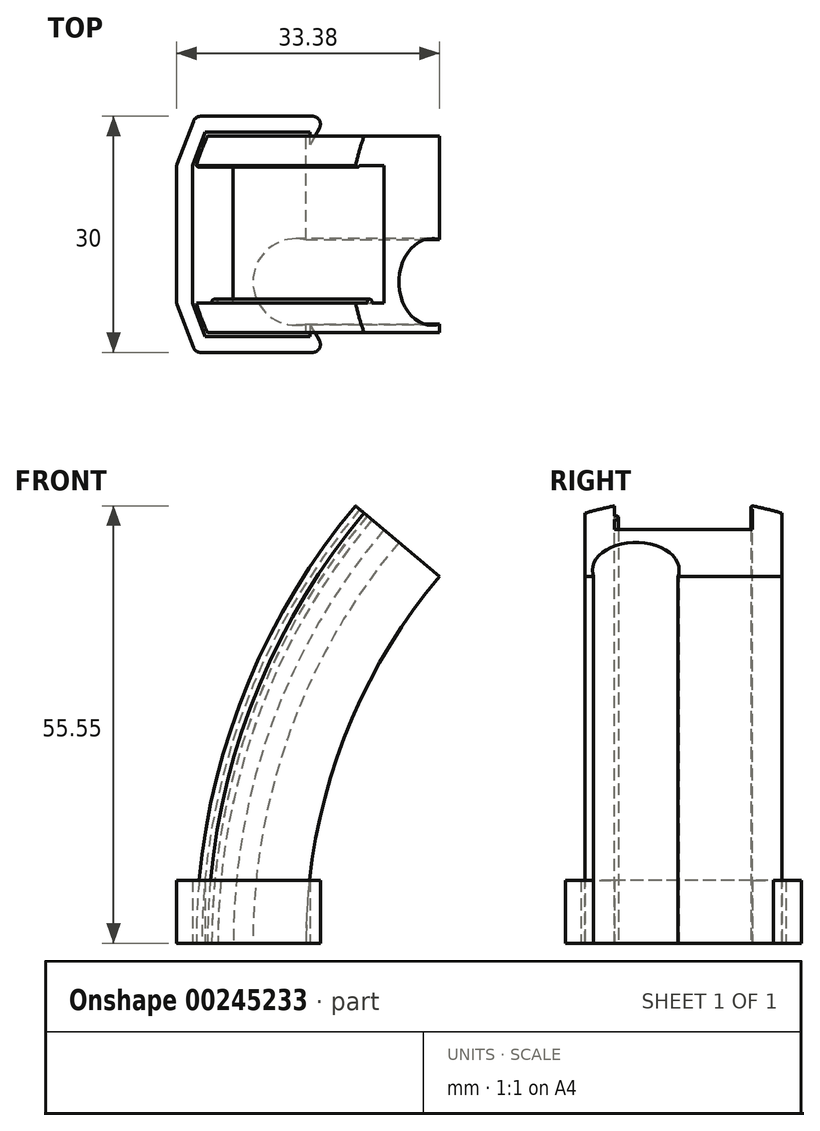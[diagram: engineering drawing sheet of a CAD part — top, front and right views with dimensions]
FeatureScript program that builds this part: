
annotation { "Feature Type Name" : "Feature", "Feature Type Description" : "" }
export const myFeature = defineFeature(function(context is Context, id is Id, definition is map)
    precondition{}
    {
        {
            var Q0;
            Q0=qCreatedBy(makeId("Front.planeOp"),FACE);
            var sketch = newSketch(context, id + "F0", { "sketchPlane" : qUnion([Q0])});
            skLineSegment(sketch, "E0", {"start": v(-8.16, 0) * mm, "end": v(70.34, 0) * mm, "construction": true});
            skArc(sketch, "E1", {"start": v(10.2, 50.46) * mm, "mid": v(-3.42, 26.85) * mm, "end": v(-8.16, 0) * mm});
            skArc(sketch, "E2", {"start": v(5.23, 54.64) * mm, "mid": v(-9.53, 29.07) * mm, "end": v(-14.66, 0) * mm});
            skLineSegment(sketch, "E3", {"start": v(10.2, 50.46) * mm, "end": v(70.34, 0) * mm, "construction": true});
            skLineSegment(sketch, "E4", {"start": v(-14.66, 0) * mm, "end": v(-8.16, 0) * mm});
            skLineSegment(sketch, "E5", {"start": v(10.2, 50.46) * mm, "end": v(5.23, 54.64) * mm});
            skSolve(sketch);
        }
        {
            var Q0;
            Q0 = qSketchRegion(id + "F0", true);
            extrude(context, id + "F1", {"entities" : qUnion([Q0]), "depth" : 25 * mm});
        }
        {
            var Q0;
            Q0=makeQuery(id+"F1.opExtrude","CAP_EDGE",EDGE,{"disambiguationData":[OSD([sQuery(id+"F0.wireOp",EDGE,"E1")])],"isStart":false});
            var Q1;
            Q1=makeQuery(id+"F1.opExtrude","CAP_VERTEX",VERTEX,{"disambiguationData":[OSD([sQuery(id+"F0.wireOp",EDGE,"E1"),sQuery(id+"F0.wireOp",EDGE,"E4")])],"isStart":false});
            cPlane(context, id + "F2", {"entities" : qUnion([Q0, Q1]), "cplaneType" : CPlaneType.CURVE_POINT, "offset" : 25 * mm, "width" : 150 * mm, "height" : 150 * mm});
        }
        {
            var Q0;
            Q0=qCreatedBy(id+"F2.planeOp",FACE);
            var sketch = newSketch(context, id + "F3", { "sketchPlane" : qUnion([Q0])});
            skPoint(sketch, "E6.0", {"position": v(-14.66, 25) * mm});
            skPoint(sketch, "E7.0", {"position": v(-8.16, 25) * mm});
            skPoint(sketch, "E8.0", {"position": v(-8.16, 12.5) * mm});
            skPoint(sketch, "E9.0", {"position": v(-14.66, 12.5) * mm});
            skLineSegment(sketch, "E10", {"start": v(-14.66, 12.5) * mm, "end": v(-8.16, 12.5) * mm, "construction": true});
            skArc(sketch, "E11", {"start": v(-14.66, 25) * mm, "mid": v(-17.39, 12.5) * mm, "end": v(-14.66, 0) * mm});
            skLineSegment(sketch, "E12", {"start": v(-14.66, 25) * mm, "end": v(-14.66, 0) * mm});
            skLineSegment(sketch, "E13", {"start": v(-8.16, 25) * mm, "end": v(-2.16, 25) * mm});
            skLineSegment(sketch, "E14.MirrorCS", {"start": v(-8.16, 0) * mm, "end": v(-2.16, 0) * mm});
            skLineSegment(sketch, "E15", {"start": v(-8.16, 25) * mm, "end": v(-8.16, 0) * mm});
            skLineSegment(sketch, "E16", {"start": v(-2.16, 25) * mm, "end": v(-2.16, 0) * mm});
            skSolve(sketch);
        }
        {
            var Q0;
            Q0=makeQuery(id+"F3.imprint","IMPRINT",FACE,{"disambiguationData":[TD([[makeQuery(id+"F3.imprint","IMPRINT",EDGE,{"derivedFrom":sQuery(id+"F3.wireOp",EDGE,"E11")}),1.0]])]});
            var Q1;
            Q1=makeQuery(id+"F3.imprint","IMPRINT",FACE,{"disambiguationData":[TD([[makeQuery(id+"F3.imprint","IMPRINT",EDGE,{"derivedFrom":sQuery(id+"F3.wireOp",EDGE,"E13")}),-1.0]])]});
            var Q2;
            Q2=makeQuery(id+"F1.opExtrude","CAP_EDGE",EDGE,{"disambiguationData":[OSD([sQuery(id+"F0.wireOp",EDGE,"E1")])],"isStart":false});
            sweep(context, id + "F4", {"operationType" : NewBodyOperationType.ADD, "profiles" : qUnion([Q0, Q1]), "path" : qUnion([Q2])});
        }
        {
            var Q0;
            {var subQ0=sQuery(id+"F0.wireOp",EDGE,"E4");var subQ1=sQuery(id+"F0.wireOp",EDGE,"E1");Q0=makeQuery(id+"F4.boolean.opBoolean","MERGE",FACE,{"derivedFrom":[makeQuery(id+"F1.opExtrude","SWEPT_FACE",FACE,{"disambiguationData":[OSD([subQ0])]}),makeQuery(id+"F4.opSweep","CAP_FACE",FACE,{"disambiguationData":[OSD([subQ1,subQ0,sQuery(id+"F3.wireOp",EDGE,"E11"),sQuery(id+"F3.wireOp",EDGE,"E12")])],"isStart":true}),makeQuery(id+"F4.opSweep","CAP_FACE",FACE,{"disambiguationData":[OSD([subQ1,subQ0,sQuery(id+"F3.wireOp",EDGE,"E13"),sQuery(id+"F3.wireOp",EDGE,"E14.MirrorCS"),sQuery(id+"F3.wireOp",EDGE,"E15"),sQuery(id+"F3.wireOp",EDGE,"OGJAd92x-gfcs-rjC3-avb7-BWxVoqmYbHhy")])],"isStart":true})]});}
            var sketch = newSketch(context, id + "F5", { "sketchPlane" : qUnion([Q0])});
            skCircle(sketch, "E17", {"center": v(-3.39, 18.55) * mm, "radius": 5.5 * mm});
            skLineSegment(sketch, "E18", {"start": v(-17.39, 12.5) * mm, "end": v(-17.39, 12.5) * mm});
            skCircle(sketch, "E19.MirrorC", {"center": v(-3.39, 6.45) * mm, "radius": 5.5 * mm});
            skLineSegment(sketch, "E20.bottom", {"start": v(-17.39, 21.25) * mm, "end": v(-11.39, 21.25) * mm});
            skLineSegment(sketch, "E20.top", {"start": v(-17.39, 3.75) * mm, "end": v(-11.39, 3.75) * mm});
            skLineSegment(sketch, "E20.left", {"start": v(-17.39, 21.25) * mm, "end": v(-17.39, 3.75) * mm});
            skLineSegment(sketch, "E20.right", {"start": v(-11.39, 21.25) * mm, "end": v(-11.39, 3.75) * mm});
            skPoint(sketch, "E20.middle", {"position": v(-14.39, 12.5) * mm});
            skLineSegment(sketch, "E21", {"start": v(-11.39, 18.75) * mm, "end": v(-3.39, 18.55) * mm, "construction": true});
            skLineSegment(sketch, "E22", {"start": v(-11.39, 18.75) * mm, "end": v(-11.39, 21.25) * mm, "construction": true});
            skSolve(sketch);
        }
        {
            var Q0;
            {var subQ0=sQuery(id+"F5.wireOp",EDGE,"E17");var subQ1=makeQuery(id+"F4.opSweep","CAP_EDGE",EDGE,{"disambiguationData":[OSD([sQuery(id+"F0.wireOp",EDGE,"E1"),sQuery(id+"F0.wireOp",EDGE,"E4"),sQuery(id+"F3.wireOp",EDGE,"OGJAd92x-gfcs-rjC3-avb7-BWxVoqmYbHhy")])],"isStart":true});var subQ2=makeQuery(id+"F5.imprint","INTERSECT",VERTEX,{"disambiguationData":[OD(0.0)],"derivedFrom":[subQ1,subQ0]});Q0=makeQuery(id+"F5.imprint","IMPRINT",FACE,{"disambiguationData":[TD([[makeQuery(id+"F5.imprint","IMPRINT",EDGE,{"disambiguationData":[TD([[subQ2,-1.0]])],"derivedFrom":subQ0}),1.0]])]});}
            var Q1;
            {var subQ0=sQuery(id+"F5.wireOp",EDGE,"E19.MirrorC");var subQ1=makeQuery(id+"F4.opSweep","CAP_EDGE",EDGE,{"disambiguationData":[OSD([sQuery(id+"F0.wireOp",EDGE,"E1"),sQuery(id+"F0.wireOp",EDGE,"E4"),sQuery(id+"F3.wireOp",EDGE,"OGJAd92x-gfcs-rjC3-avb7-BWxVoqmYbHhy")])],"isStart":true});var subQ2=makeQuery(id+"F5.imprint","INTERSECT",VERTEX,{"disambiguationData":[OD(0.0)],"derivedFrom":[subQ1,subQ0]});Q1=makeQuery(id+"F5.imprint","IMPRINT",FACE,{"disambiguationData":[TD([[makeQuery(id+"F5.imprint","IMPRINT",EDGE,{"disambiguationData":[TD([[subQ2,-1.0]])],"derivedFrom":subQ0}),-1.0]])]});}
            var Q2;
            {var subQ4=sQuery(id+"F5.wireOp",EDGE,"E20.right");Q2=makeQuery(id+"F5.imprint","IMPRINT",FACE,{"disambiguationData":[TD([[makeQuery(id+"F5.imprint","IMPRINT",EDGE,{"derivedFrom":subQ4}),-1.0]])]});}
            var Q3;
            {var subQ0=sQuery(id+"F5.wireOp",EDGE,"E19.MirrorC");var subQ1=makeQuery(id+"F4.opSweep","CAP_EDGE",EDGE,{"disambiguationData":[OSD([sQuery(id+"F0.wireOp",EDGE,"E1"),sQuery(id+"F0.wireOp",EDGE,"E4"),sQuery(id+"F3.wireOp",EDGE,"E16")])],"isStart":true});var subQ2=makeQuery(id+"F5.imprint","INTERSECT",VERTEX,{"disambiguationData":[OD(0.0)],"derivedFrom":[subQ1,subQ0]});Q3=makeQuery(id+"F5.imprint","IMPRINT",FACE,{"disambiguationData":[TD([[makeQuery(id+"F5.imprint","IMPRINT",EDGE,{"disambiguationData":[TD([[subQ2,-1.0]])],"derivedFrom":subQ0}),-1.0]])]});}
            var Q4;
            {var subQ0=sQuery(id+"F5.wireOp",EDGE,"E17");var subQ1=makeQuery(id+"F4.opSweep","CAP_EDGE",EDGE,{"disambiguationData":[OSD([sQuery(id+"F0.wireOp",EDGE,"E1"),sQuery(id+"F0.wireOp",EDGE,"E4"),sQuery(id+"F3.wireOp",EDGE,"E16")])],"isStart":true});var subQ2=makeQuery(id+"F5.imprint","INTERSECT",VERTEX,{"disambiguationData":[OD(0.0)],"derivedFrom":[subQ1,subQ0]});Q4=makeQuery(id+"F5.imprint","IMPRINT",FACE,{"disambiguationData":[TD([[makeQuery(id+"F5.imprint","IMPRINT",EDGE,{"disambiguationData":[TD([[subQ2,-1.0]])],"derivedFrom":subQ0}),1.0]])]});}
            var Q5;
            Q5=makeQuery(id+"F4.opSweep","SWEPT_EDGE",EDGE,{"disambiguationData":[OSD([sQuery(id+"F0.wireOp",EDGE,"E1"),sQuery(id+"F3.wireOp",EDGE,"E13"),sQuery(id+"F3.wireOp",EDGE,"OGJAd92x-gfcs-rjC3-avb7-BWxVoqmYbHhy")])]});
            sweep(context, id + "F6", {"operationType" : NewBodyOperationType.REMOVE, "profiles" : qUnion([Q0, Q1, Q2, Q3, Q4]), "path" : qUnion([Q5])});
        }
        {
            var Q0;
            {var subQ0=sQuery(id+"F0.wireOp",EDGE,"E4");var subQ1=sQuery(id+"F0.wireOp",EDGE,"E1");Q0=makeQuery(id+"F4.boolean.opBoolean","MERGE",FACE,{"derivedFrom":[makeQuery(id+"F1.opExtrude","SWEPT_FACE",FACE,{"disambiguationData":[OSD([subQ0])]}),makeQuery(id+"F4.opSweep","CAP_FACE",FACE,{"disambiguationData":[OSD([subQ1,subQ0,sQuery(id+"F3.wireOp",EDGE,"E11"),sQuery(id+"F3.wireOp",EDGE,"E12")])],"isStart":true}),makeQuery(id+"F4.opSweep","CAP_FACE",FACE,{"disambiguationData":[OSD([subQ1,subQ0,sQuery(id+"F3.wireOp",EDGE,"E13"),sQuery(id+"F3.wireOp",EDGE,"E14.MirrorCS"),sQuery(id+"F3.wireOp",EDGE,"E15"),sQuery(id+"F3.wireOp",EDGE,"OGJAd92x-gfcs-rjC3-avb7-BWxVoqmYbHhy")])],"isStart":true})]});}
            var sketch = newSketch(context, id + "F7", { "sketchPlane" : qUnion([Q0])});
            skPoint(sketch, "E23.startSnap0", {"position": v(-15.43, 1.85) * mm});
            skArc(sketch, "E24", {"start": v(-15.38, 3.75) * mm, "mid": v(-15.73, 3.96) * mm, "end": v(-16.08, 3.75) * mm});
            skLineSegment(sketch, "E25", {"start": v(-15.73, 3.96) * mm, "end": v(-15.73, 3.56) * mm, "construction": true});
            skLineSegment(sketch, "E26", {"start": v(-13.73, 20.73) * mm, "end": v(-13.73, 21.13) * mm, "construction": true});
            skArc(sketch, "E27", {"start": v(-14.12, 21.25) * mm, "mid": v(-13.73, 20.73) * mm, "end": v(-13.35, 21.25) * mm});
            skPoint(sketch, "E28", {"position": v(-13.73, 21.25) * mm});
            skLineSegment(sketch, "E29", {"start": v(-16.08, 3.75) * mm, "end": v(-15.38, 3.75) * mm});
            skLineSegment(sketch, "E30", {"start": v(-14.12, 21.25) * mm, "end": v(-13.35, 21.25) * mm});
            skSolve(sketch);
        }
        {
            var Q0;
            Q0=makeQuery(id+"F7.imprint","IMPRINT",FACE,{"disambiguationData":[TD([[makeQuery(id+"F7.imprint","IMPRINT",EDGE,{"derivedFrom":sQuery(id+"F7.wireOp",EDGE,"E24")}),1.0]])]});
            var Q1;
            Q1=makeQuery(id+"F7.imprint","IMPRINT",FACE,{"disambiguationData":[TD([[makeQuery(id+"F7.imprint","IMPRINT",EDGE,{"derivedFrom":sQuery(id+"F7.wireOp",EDGE,"E27")}),1.0]])]});
            var Q2;
            Q2=makeQuery(id+"F4.opSweep","SWEPT_EDGE",EDGE,{"disambiguationData":[OSD([sQuery(id+"F0.wireOp",EDGE,"E1"),sQuery(id+"F3.wireOp",EDGE,"E13"),sQuery(id+"F3.wireOp",EDGE,"OGJAd92x-gfcs-rjC3-avb7-BWxVoqmYbHhy")])]});
            sweep(context, id + "F8", {"operationType" : NewBodyOperationType.ADD, "profiles" : qUnion([Q0, Q1]), "path" : qUnion([Q2])});
        }
        {
            var Q0;
            Q0=qCreatedBy(id+"F2.planeOp",FACE);
            var sketch = newSketch(context, id + "F9", { "sketchPlane" : qUnion([Q0])});
            skLineSegment(sketch, "E31.bottom", {"start": v(0, 29.33) * mm, "end": v(-21.73, 29.33) * mm});
            skLineSegment(sketch, "E31.top", {"start": v(0, -4.96) * mm, "end": v(-21.73, -4.96) * mm});
            skLineSegment(sketch, "E31.left", {"start": v(0, 29.33) * mm, "end": v(0, -4.96) * mm});
            skLineSegment(sketch, "E31.right", {"start": v(-21.73, 29.33) * mm, "end": v(-21.73, -4.96) * mm});
            skPoint(sketch, "E31.middle", {"position": v(-10.86, 12.19) * mm});
            skSolve(sketch);
        }
        {
            var Q0;
            Q0=qCreatedBy(id+"F2.planeOp",FACE);
            var sketch = newSketch(context, id + "F10", { "sketchPlane" : qUnion([Q0])});
            skPoint(sketch, "E32.0", {"position": v(-2.16, 23.9) * mm});
            skPoint(sketch, "E33.0", {"position": v(-2.16, 25) * mm});
            skPoint(sketch, "E34.0", {"position": v(-14.66, 25) * mm});
            skPoint(sketch, "E35.0", {"position": v(-16.08, 21.25) * mm});
            skPoint(sketch, "E36.0", {"position": v(-11.39, 12.5) * mm});
            skPoint(sketch, "E37.0", {"position": v(-2.16, 12.5) * mm});
            skLineSegment(sketch, "E38", {"start": v(-2.16, 12.5) * mm, "end": v(-11.39, 12.5) * mm, "construction": true});
            skLineSegment(sketch, "E39", {"start": v(-2.16, 23.9) * mm, "end": v(-1.66, 23.9) * mm, "construction": true});
            skLineSegment(sketch, "E40", {"start": v(-1.66, 23.9) * mm, "end": v(-1.66, 25) * mm});
            skLineSegment(sketch, "E41", {"start": v(-1.66, 25) * mm, "end": v(-1.66, 25.5) * mm});
            skLineSegment(sketch, "E42", {"start": v(-1.66, 25.5) * mm, "end": v(-14.97, 25.5) * mm});
            skLineSegment(sketch, "E43", {"start": v(-14.97, 25.5) * mm, "end": v(-15.16, 25) * mm});
            skLineSegment(sketch, "E44", {"start": v(-15.16, 25) * mm, "end": v(-14.66, 25) * mm, "construction": true});
            skLineSegment(sketch, "E45", {"start": v(-15.16, 25) * mm, "end": v(-16.58, 21.25) * mm});
            skLineSegment(sketch, "E46", {"start": v(-16.08, 21.25) * mm, "end": v(-16.58, 21.25) * mm, "construction": true});
            skLineSegment(sketch, "E47", {"start": v(-16.08, 21.25) * mm, "end": v(-16.08, 12.5) * mm, "construction": true});
            skLineSegment(sketch, "E48", {"start": v(-16.58, 21.25) * mm, "end": v(-16.58, 12.5) * mm});
            skLineSegment(sketch, "E49", {"start": v(-16.58, 12.5) * mm, "end": v(-18.58, 12.5) * mm, "construction": true});
            skLineSegment(sketch, "E50", {"start": v(-18.58, 12.5) * mm, "end": v(-18.58, 21.25) * mm});
            skLineSegment(sketch, "E51", {"start": v(-18.58, 21.25) * mm, "end": v(-16.97, 25.5) * mm});
            skLineSegment(sketch, "E52", {"start": v(-16.97, 25.5) * mm, "end": v(-16.2, 27.5) * mm});
            skLineSegment(sketch, "E53", {"start": v(-14.97, 25.5) * mm, "end": v(-14.97, 27.5) * mm, "construction": true});
            skLineSegment(sketch, "E54", {"start": v(-16.2, 27.5) * mm, "end": v(0.42, 27.5) * mm});
            skLineSegment(sketch, "E55", {"start": v(0.42, 27.5) * mm, "end": v(-1.66, 23.9) * mm});
            skLineSegment(sketch, "E56.MirrorCS", {"start": v(-16.58, 3.75) * mm, "end": v(-16.58, 12.5) * mm});
            skLineSegment(sketch, "E57.MirrorCS", {"start": v(-18.58, 12.5) * mm, "end": v(-18.58, 3.75) * mm});
            skLineSegment(sketch, "E58.MirrorCS", {"start": v(-18.58, 3.75) * mm, "end": v(-16.97, -0.5) * mm});
            skLineSegment(sketch, "E59.MirrorCS", {"start": v(-15.16, 0) * mm, "end": v(-16.58, 3.75) * mm});
            skLineSegment(sketch, "E60.MirrorCS", {"start": v(-14.97, -0.5) * mm, "end": v(-15.16, 0) * mm});
            skLineSegment(sketch, "E61.MirrorCS", {"start": v(-16.97, -0.5) * mm, "end": v(-16.2, -2.5) * mm});
            skLineSegment(sketch, "E62.MirrorCS", {"start": v(-16.2, -2.5) * mm, "end": v(0.42, -2.5) * mm});
            skLineSegment(sketch, "E63.MirrorCS", {"start": v(-1.66, 0) * mm, "end": v(-1.66, -0.5) * mm});
            skLineSegment(sketch, "E64.MirrorCS", {"start": v(-1.66, 1.1) * mm, "end": v(-1.66, 0) * mm});
            skLineSegment(sketch, "E65.MirrorCS", {"start": v(0.42, -2.5) * mm, "end": v(-1.66, 1.1) * mm});
            skLineSegment(sketch, "E66.MirrorCS", {"start": v(-1.66, -0.5) * mm, "end": v(-14.97, -0.5) * mm});
            skSolve(sketch);
        }
        {
            var Q0;
            Q0 = qSketchRegion(id + "F10", true);
            extrude(context, id + "F11", {"entities" : qUnion([Q0]), "operationType" : NewBodyOperationType.ADD, "oppositeDirection" : true, "depth" : 8 * mm});
        }
        {
            var Q0;
            Q0=makeQuery(id+"F11.opExtrude","SWEPT_EDGE",EDGE,{"disambiguationData":[OSD([sQuery(id+"F10.wireOp",EDGE,"E54"),sQuery(id+"F10.wireOp",EDGE,"E55")])]});
            var Q1;
            Q1=makeQuery(id+"F11.opExtrude","SWEPT_EDGE",EDGE,{"disambiguationData":[OSD([sQuery(id+"F10.wireOp",EDGE,"E62.MirrorCS"),sQuery(id+"F10.wireOp",EDGE,"E65.MirrorCS")])]});
            var Q2;
            Q2=makeQuery(id+"F11.opExtrude","SWEPT_EDGE",EDGE,{"disambiguationData":[OSD([sQuery(id+"F10.wireOp",EDGE,"E61.MirrorCS"),sQuery(id+"F10.wireOp",EDGE,"E62.MirrorCS")])]});
            var Q3;
            Q3=makeQuery(id+"F11.opExtrude","SWEPT_EDGE",EDGE,{"disambiguationData":[OSD([sQuery(id+"F10.wireOp",EDGE,"E57.MirrorCS"),sQuery(id+"F10.wireOp",EDGE,"E58.MirrorCS")])]});
            var Q4;
            Q4=makeQuery(id+"F11.opExtrude","SWEPT_EDGE",EDGE,{"disambiguationData":[OSD([sQuery(id+"F10.wireOp",EDGE,"E50"),sQuery(id+"F10.wireOp",EDGE,"E51")])]});
            var Q5;
            Q5=makeQuery(id+"F11.opExtrude","SWEPT_EDGE",EDGE,{"disambiguationData":[OSD([sQuery(id+"F10.wireOp",EDGE,"E52"),sQuery(id+"F10.wireOp",EDGE,"E54")])]});
            fillet(context, id + "F12", {"entities" : qUnion([Q0, Q1, Q2, Q3, Q4, Q5]), "radius" : 1 * mm, "tangentPropagation" : true, "allowEdgeOverflow" : false});
        }
    });
